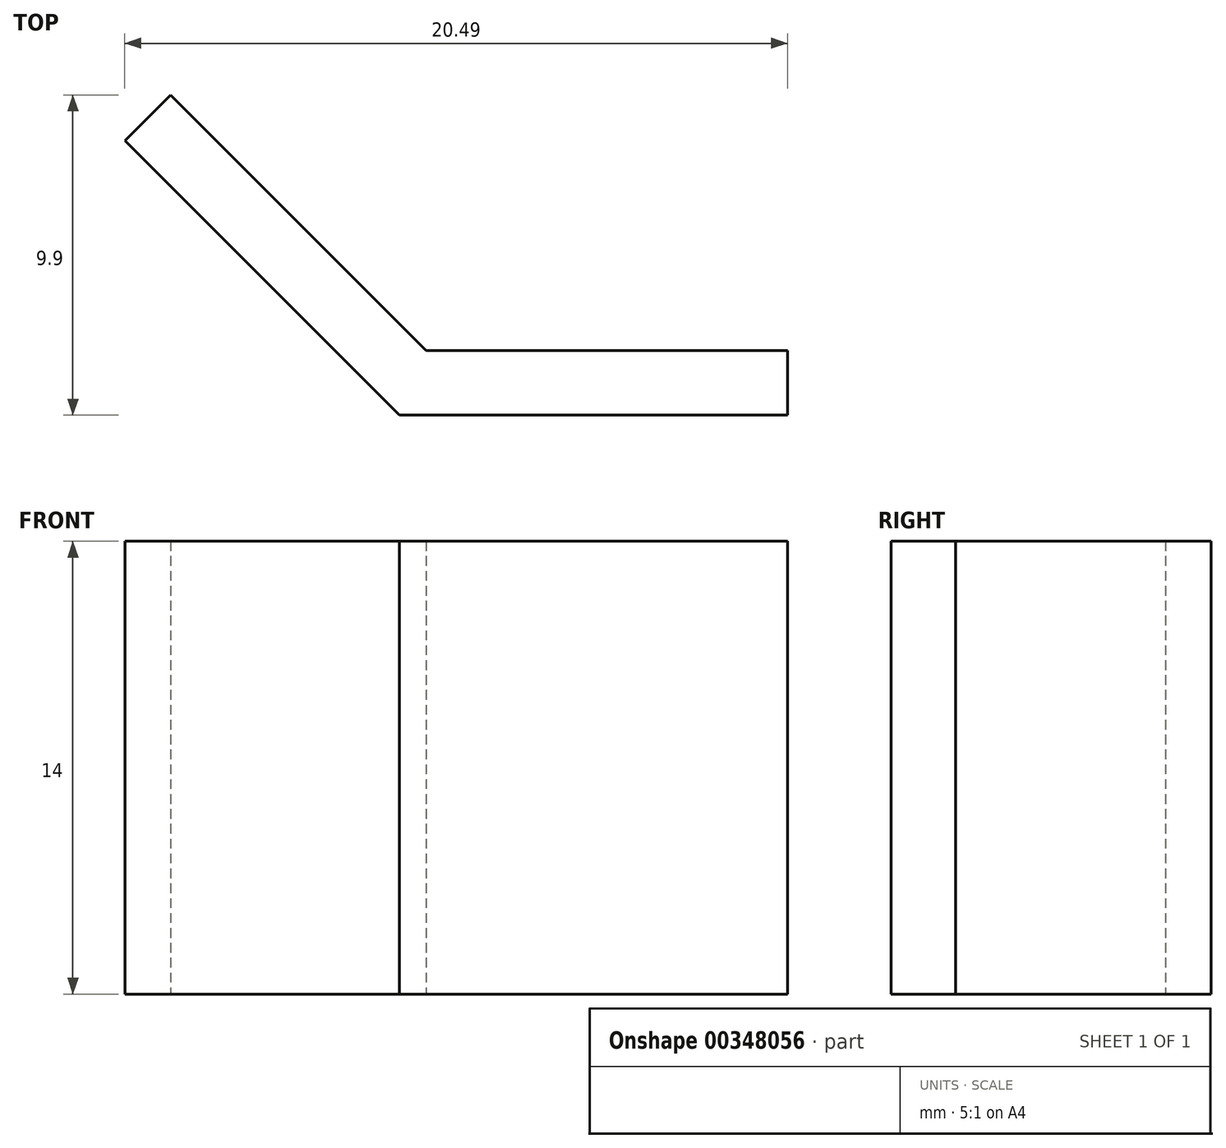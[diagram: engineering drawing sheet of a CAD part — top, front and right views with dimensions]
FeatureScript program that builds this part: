
annotation { "Feature Type Name" : "Feature", "Feature Type Description" : "" }
export const myFeature = defineFeature(function(context is Context, id is Id, definition is map)
    precondition{}
    {
        {
            var Q0;
            Q0=qCreatedBy(makeId("Top.planeOp"),FACE);
            var sketch = newSketch(context, id + "F0", { "sketchPlane" : qUnion([Q0])});
            skLineSegment(sketch, "E0", {"start": v(-8.49, 8.49) * mm, "end": v(0, 0) * mm});
            skLineSegment(sketch, "E1", {"start": v(0, 0) * mm, "end": v(12, 0) * mm});
            skLineSegment(sketch, "E2", {"start": v(-8.49, 8.49) * mm, "end": v(-7.07, 9.9) * mm});
            skLineSegment(sketch, "E3", {"start": v(-7.07, 9.9) * mm, "end": v(0.83, 2) * mm});
            skLineSegment(sketch, "E4", {"start": v(0.83, 2) * mm, "end": v(12, 2) * mm});
            skLineSegment(sketch, "E5", {"start": v(12, 2) * mm, "end": v(12, 0) * mm});
            skLineSegment(sketch, "E6", {"start": v(0, 0) * mm, "end": v(0.83, 2) * mm, "construction": true});
            skSolve(sketch);
        }
        {
            var Q0;
            Q0=makeQuery(id+"F0.imprint","IMPRINT",FACE,{"disambiguationData":[TD([[makeQuery(id+"F0.imprint","IMPRINT",EDGE,{"derivedFrom":sQuery(id+"F0.wireOp",EDGE,"E0")}),1.0]])]});
            extrude(context, id + "F1", {"entities" : qUnion([Q0]), "depth" : 14 * mm});
        }
    });
